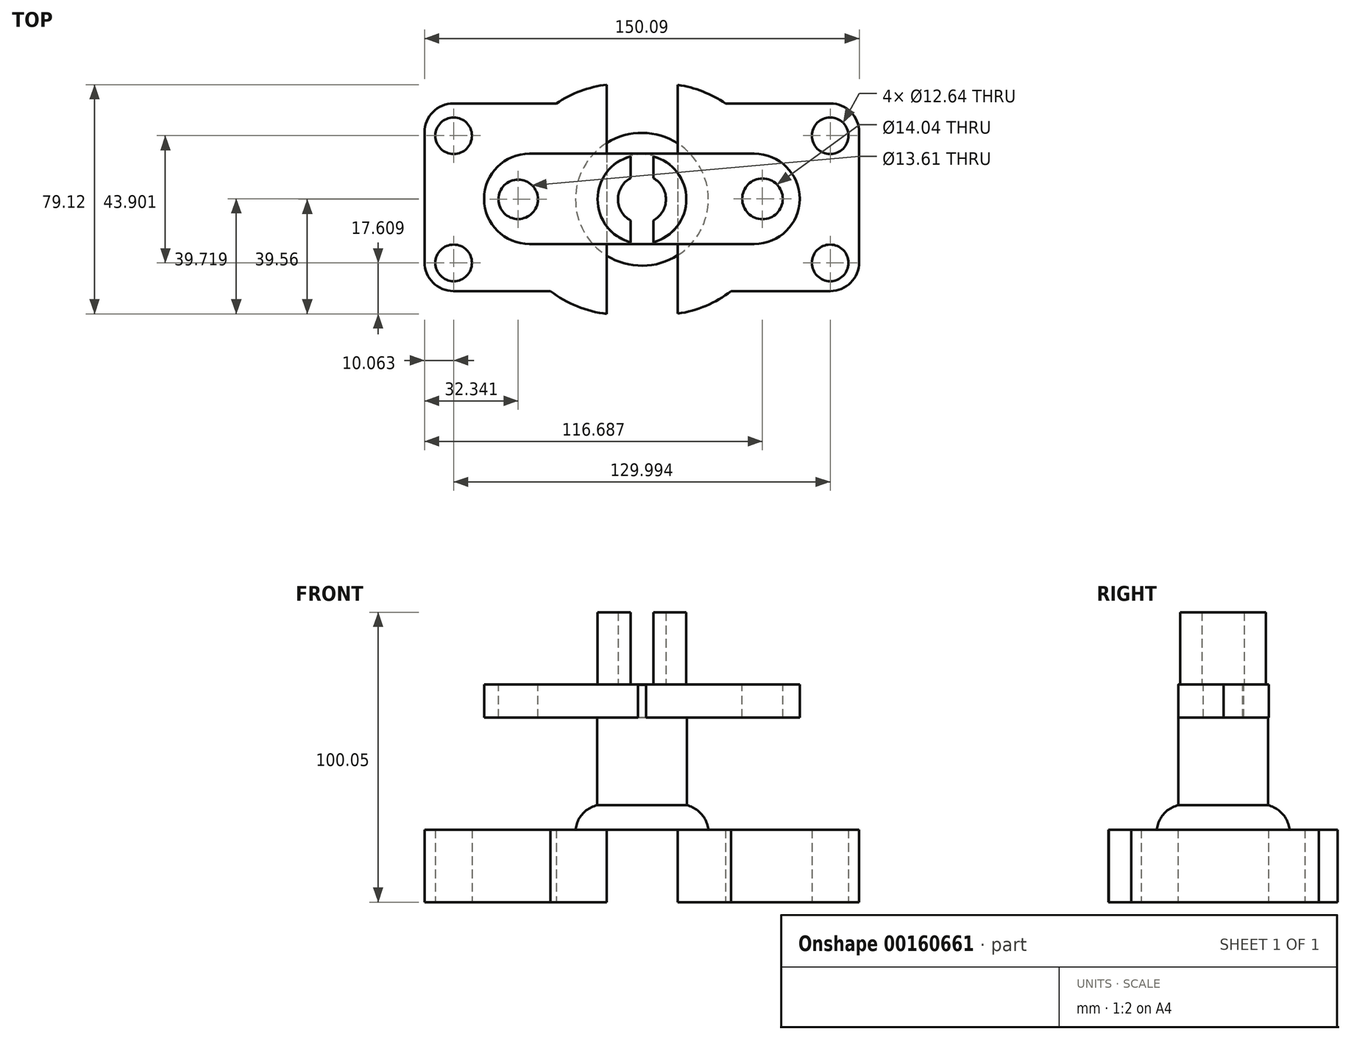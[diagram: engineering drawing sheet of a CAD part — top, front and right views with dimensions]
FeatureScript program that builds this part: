
annotation { "Feature Type Name" : "Feature", "Feature Type Description" : "" }
export const myFeature = defineFeature(function(context is Context, id is Id, definition is map)
    precondition{}
    {
        {
            var Q0;
            Q0=qCreatedBy(makeId("Top.planeOp"),FACE);
            var sketch = newSketch(context, id + "F0", { "sketchPlane" : qUnion([Q0])});
            skLineSegment(sketch, "E0.left", {"start": v(-75.06, 33.1) * mm, "end": v(-75.06, -31.69) * mm});
            skLineSegment(sketch, "E0.right", {"start": v(75.03, 33.1) * mm, "end": v(75.03, -31.69) * mm});
            skLineSegment(sketch, "E1", {"start": v(-12.1, 39.56) * mm, "end": v(-12.1, -39.56) * mm});
            skLineSegment(sketch, "E2", {"start": v(12.4, 39.47) * mm, "end": v(12.4, -39.47) * mm});
            skLineSegment(sketch, "E3.left", {"start": v(75.03, 22.97) * mm, "end": v(75.03, -23.34) * mm});
            skCircle(sketch, "E4", {"center": v(-65, -21.95) * mm, "radius": 6.32 * mm});
            skCircle(sketch, "E5.MirrorC", {"center": v(65, -21.95) * mm, "radius": 6.32 * mm});
            skLineSegment(sketch, "E6", {"start": v(-12.1, 33.1) * mm, "end": v(-12.1, 39.56) * mm});
            skLineSegment(sketch, "E7", {"start": v(12.4, 33.1) * mm, "end": v(12.4, 39.47) * mm});
            skLineSegment(sketch, "E8", {"start": v(-12.1, -31.69) * mm, "end": v(-12.1, -39.56) * mm});
            skLineSegment(sketch, "E9", {"start": v(12.4, -31.69) * mm, "end": v(12.4, -39.47) * mm});
            skLineSegment(sketch, "E10", {"start": v(-75.06, 33.1) * mm, "end": v(-12.1, 33.1) * mm});
            skLineSegment(sketch, "E11", {"start": v(-75.06, -31.69) * mm, "end": v(-12.1, -31.69) * mm});
            skLineSegment(sketch, "E12", {"start": v(12.4, -31.69) * mm, "end": v(75.03, -31.69) * mm});
            skLineSegment(sketch, "E13", {"start": v(12.4, 33.1) * mm, "end": v(75.03, 33.1) * mm});
            skArc(sketch, "E14", {"start": v(12.4, -39.47) * mm, "mid": v(46.48, 0) * mm, "end": v(12.4, 39.47) * mm});
            skArc(sketch, "E15", {"start": v(-12.1, 39.56) * mm, "mid": v(-47.24, 0) * mm, "end": v(-12.1, -39.56) * mm});
            skCircle(sketch, "E16.MirrorC", {"center": v(-65, 21.95) * mm, "radius": 6.32 * mm});
            skCircle(sketch, "E17.MirrorC", {"center": v(65, 21.95) * mm, "radius": 6.32 * mm});
            skSolve(sketch);
        }
        {
            var Q0;
            Q0 = qSketchRegion(id + "F0", true);
            extrude(context, id + "F1", {"entities" : qUnion([Q0]), "depth" : 25 * mm});
        }
        {
            var Q0;
            Q0=makeQuery(id+"F1.opExtrude","SWEPT_EDGE",EDGE,{"disambiguationData":[OSD([sQuery(id+"F0.wireOp",EDGE,"E0.left"),sQuery(id+"F0.wireOp",EDGE,"E10")])]});
            var Q1;
            Q1=makeQuery(id+"F1.opExtrude","SWEPT_EDGE",EDGE,{"disambiguationData":[OSD([sQuery(id+"F0.wireOp",EDGE,"E0.left"),sQuery(id+"F0.wireOp",EDGE,"E11")])]});
            var Q2;
            Q2=makeQuery(id+"F1.opExtrude","SWEPT_EDGE",EDGE,{"disambiguationData":[OSD([sQuery(id+"F0.wireOp",EDGE,"E0.right"),sQuery(id+"F0.wireOp",EDGE,"E13")])]});
            var Q3;
            Q3=makeQuery(id+"F1.opExtrude","SWEPT_EDGE",EDGE,{"disambiguationData":[OSD([sQuery(id+"F0.wireOp",EDGE,"E0.right"),sQuery(id+"F0.wireOp",EDGE,"E12")])]});
            fillet(context, id + "F2", {"entities" : qUnion([Q0, Q1, Q2, Q3]), "radius" : 10 * mm, "tangentPropagation" : true, "allowEdgeOverflow" : false});
        }
        {
            var Q0;
            Q0=qCreatedBy(makeId("Right.planeOp"),FACE);
            var sketch = newSketch(context, id + "F3", { "sketchPlane" : qUnion([Q0])});
            skLineSegment(sketch, "E18.bottom", {"start": v(0, 75.05) * mm, "end": v(-15.51, 75.05) * mm});
            skLineSegment(sketch, "E18.top", {"start": v(0, 24.98) * mm, "end": v(-15.51, 24.98) * mm});
            skLineSegment(sketch, "E18.left", {"start": v(0, 75.05) * mm, "end": v(0, 24.98) * mm});
            skLineSegment(sketch, "E18.right", {"start": v(-15.51, 75.05) * mm, "end": v(-15.51, 24.98) * mm});
            skArc(sketch, "E19", {"start": v(-15.51, 33.44) * mm, "mid": v(-20.56, 30.39) * mm, "end": v(-22.92, 24.98) * mm});
            skLineSegment(sketch, "E20", {"start": v(-22.92, 24.98) * mm, "end": v(-15.51, 24.98) * mm});
            skLineSegment(sketch, "E21", {"start": v(-15.51, 33.44) * mm, "end": v(-15.51, 24.98) * mm});
            skSolve(sketch);
        }
        {
            var Q0;
            Q0=makeQuery(id+"F3.imprint","IMPRINT",FACE,{"disambiguationData":[TD([[makeQuery(id+"F3.imprint","IMPRINT",EDGE,{"derivedFrom":sQuery(id+"F3.wireOp",EDGE,"E19")}),1.0]])]});
            var Q1;
            Q1=makeQuery(id+"F3.imprint","IMPRINT",FACE,{"disambiguationData":[TD([[makeQuery(id+"F3.imprint","IMPRINT",EDGE,{"derivedFrom":sQuery(id+"F3.wireOp",EDGE,"E18.bottom")}),1.0]])]});
            var Q2;
            Q2=sQuery(id+"F3.wireOp",EDGE,"E18.left");
            revolve(context, id + "F4", {"entities" : qUnion([Q0, Q1]), "axis" : qUnion([Q2]), "revolveType" : RevolveType.FULL});
        }
        {
            var Q0;
            Q0=makeQuery(id+"F4.opRevolve","SWEPT_FACE",FACE,{"disambiguationData":[OSD([sQuery(id+"F3.wireOp",EDGE,"E18.bottom")])]});
            var sketch = newSketch(context, id + "F5", { "sketchPlane" : qUnion([Q0])});
            skCircle(sketch, "E22", {"center": v(0, 0) * mm, "radius": 8.28 * mm});
            skCircle(sketch, "E23", {"center": v(0, 0) * mm, "radius": 15.31 * mm});
            skLineSegment(sketch, "E24", {"start": v(-3.94, 7.28) * mm, "end": v(-3.94, 14.8) * mm});
            skLineSegment(sketch, "E25", {"start": v(3.94, 7.28) * mm, "end": v(3.94, 14.8) * mm});
            skLineSegment(sketch, "E26", {"start": v(-3.94, -7.28) * mm, "end": v(-3.94, -14.8) * mm});
            skLineSegment(sketch, "E27", {"start": v(3.94, -7.28) * mm, "end": v(3.94, -14.8) * mm});
            skSolve(sketch);
        }
        {
            var Q0;
            {var subQ0=sQuery(id+"F5.wireOp",EDGE,"E24");Q0=makeQuery(id+"F5.imprint","IMPRINT",FACE,{"disambiguationData":[TD([[makeQuery(id+"F5.imprint","IMPRINT",EDGE,{"derivedFrom":subQ0}),1.0]])]});}
            var Q1;
            {var subQ0=sQuery(id+"F5.wireOp",EDGE,"E25");Q1=makeQuery(id+"F5.imprint","IMPRINT",FACE,{"disambiguationData":[TD([[makeQuery(id+"F5.imprint","IMPRINT",EDGE,{"derivedFrom":subQ0}),-1.0]])]});}
            extrude(context, id + "F6", {"entities" : qUnion([Q0, Q1]), "operationType" : NewBodyOperationType.ADD, "depth" : 25 * mm});
        }
        {
            var Q0;
            Q0=qCreatedBy(makeId("Right.planeOp"),FACE);
            var sketch = newSketch(context, id + "F7", { "sketchPlane" : qUnion([Q0])});
            skLineSegment(sketch, "E28.bottom", {"start": v(15.77, 75.12) * mm, "end": v(-15.45, 75.12) * mm});
            skLineSegment(sketch, "E28.top", {"start": v(15.77, 63.65) * mm, "end": v(-15.45, 63.65) * mm});
            skLineSegment(sketch, "E28.left", {"start": v(15.77, 75.12) * mm, "end": v(15.77, 63.65) * mm});
            skLineSegment(sketch, "E28.right", {"start": v(-15.45, 75.12) * mm, "end": v(-15.45, 63.65) * mm});
            skSolve(sketch);
        }
        {
            var Q0;
            Q0 = qSketchRegion(id + "F7", true);
            extrude(context, id + "F8", {"entities" : qUnion([Q0]), "operationType" : NewBodyOperationType.ADD, "endBound" : BoundingType.SYMMETRIC, "depth" : 109 * mm});
        }
        {
            var Q0;
            Q0=makeQuery(id+"F8.opExtrude","CAP_EDGE",EDGE,{"disambiguationData":[OSD([sQuery(id+"F7.wireOp",EDGE,"E28.right")])],"isStart":false});
            var Q1;
            Q1=makeQuery(id+"F8.opExtrude","CAP_EDGE",EDGE,{"disambiguationData":[OSD([sQuery(id+"F7.wireOp",EDGE,"E28.left")])],"isStart":false});
            fillet(context, id + "F9", {"entities" : qUnion([Q0, Q1]), "radius" : 15.7 * mm, "tangentPropagation" : true, "allowEdgeOverflow" : false});
        }
        {
            var Q0;
            Q0=makeQuery(id+"F8.opExtrude","CAP_EDGE",EDGE,{"disambiguationData":[OSD([sQuery(id+"F7.wireOp",EDGE,"E28.right")])],"isStart":true});
            var Q1;
            Q1=makeQuery(id+"F8.opExtrude","CAP_EDGE",EDGE,{"disambiguationData":[OSD([sQuery(id+"F7.wireOp",EDGE,"E28.left")])],"isStart":true});
            fillet(context, id + "F10", {"entities" : qUnion([Q0, Q1]), "radius" : 15.7 * mm, "tangentPropagation" : true, "allowEdgeOverflow" : false});
        }
        {
            var Q0;
            Q0=makeQuery(id+"F8.opExtrude","SWEPT_FACE",FACE,{"disambiguationData":[OSD([sQuery(id+"F7.wireOp",EDGE,"E28.bottom")])]});
            var sketch = newSketch(context, id + "F11", { "sketchPlane" : qUnion([Q0])});
            skCircle(sketch, "E29", {"center": v(-42.72, 0) * mm, "radius": 6.8 * mm});
            skCircle(sketch, "E30", {"center": v(41.63, 0.16) * mm, "radius": 7.02 * mm});
            skSolve(sketch);
        }
        {
            var Q0;
            Q0 = qSketchRegion(id + "F11", true);
            extrude(context, id + "F12", {"entities" : qUnion([Q0]), "operationType" : NewBodyOperationType.REMOVE, "oppositeDirection" : true, "depth" : 14.5 * mm});
        }
    });
